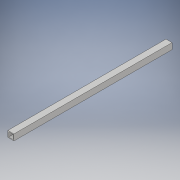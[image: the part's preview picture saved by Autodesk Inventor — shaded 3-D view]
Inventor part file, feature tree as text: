
AUTODESK INVENTOR PART (.ipt)
format: ipt  version: 2018 (Build 220112000, 112)  size: 105,472 bytes
history: native  units: in
note: dims shown in document units (in); Inventor stores cm internally (conversion verified against a paired STEP export)
features: extrude x2, sketch x2
ambient origin geometry x8: Origin, YZ Plane, XZ Plane, XY Plane, X Axis, Y Axis, Z Axis, Center Point
bodies: Solid1 (feature_tree)
feature tree (4):
  extrude  "Extrusion1"  Depth=26.0in
  extrude  "Extrusion2"  Depth=0.125in
  sketch  "Sketch1"  dims[d0=1.0in d1=26.0in]
  sketch  "Sketch2"  dims[d2=1.0in d3=0.0in d4=0.125in d5=0.125in d6=0.75in d7=0.75in d8=26.8125in d9=0.0in]
